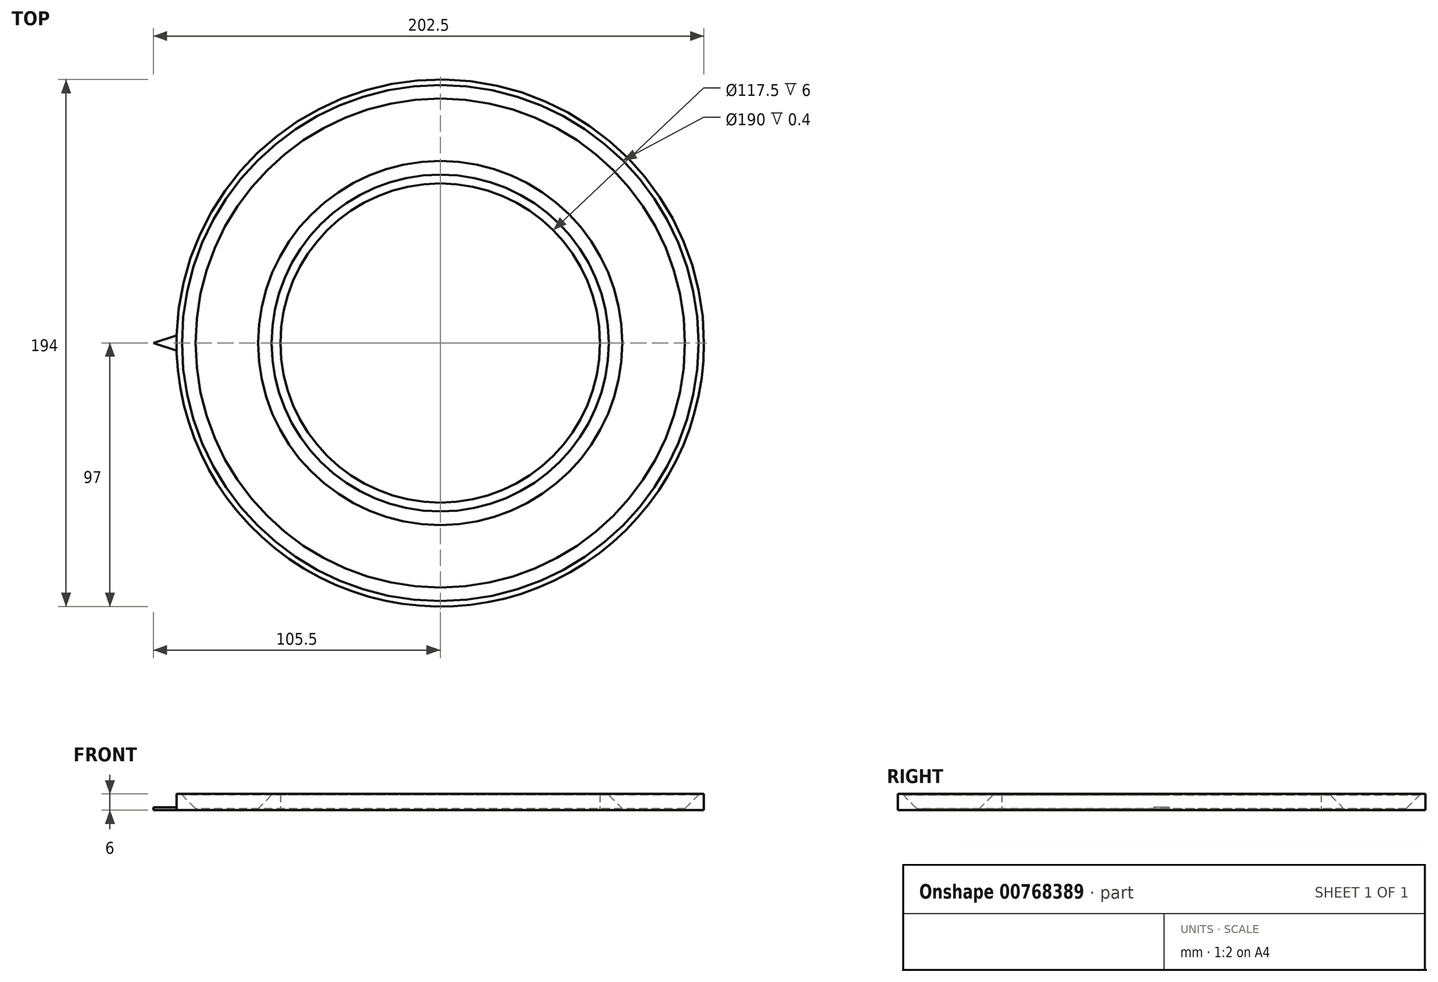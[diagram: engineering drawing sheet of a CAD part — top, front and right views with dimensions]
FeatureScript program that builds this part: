
annotation { "Feature Type Name" : "Feature", "Feature Type Description" : "" }
export const myFeature = defineFeature(function(context is Context, id is Id, definition is map)
    precondition{}
    {
        {
            var Q0;
            Q0=qCreatedBy(makeId("Top.planeOp"),FACE);
            var sketch = newSketch(context, id + "F0", { "sketchPlane" : qUnion([Q0])});
            skCircle(sketch, "E0", {"center": v(0, 0) * mm, "radius": 58.75 * mm});
            skCircle(sketch, "E1", {"center": v(0, 0) * mm, "radius": 62 * mm});
            skCircle(sketch, "E2", {"center": v(0, 0) * mm, "radius": 97 * mm});
            skCircle(sketch, "E3", {"center": v(0, 0) * mm, "radius": 95 * mm});
            skLineSegment(sketch, "E4", {"start": v(-97, 0) * mm, "end": v(-105.5, 0) * mm});
            skLineSegment(sketch, "E5", {"start": v(-105.5, 0) * mm, "end": v(-96.96, 2.84) * mm});
            skLineSegment(sketch, "E6", {"start": v(-105.5, 0) * mm, "end": v(-96.96, -2.84) * mm});
            skSolve(sketch);
        }
        {
            var Q0;
            Q0=makeQuery(id+"F0.imprint","IMPRINT",FACE,{"disambiguationData":[TD([[makeQuery(id+"F0.imprint","IMPRINT",EDGE,{"derivedFrom":sQuery(id+"F0.wireOp",EDGE,"E0")}),-1.0]])]});
            var Q1;
            Q1=makeQuery(id+"F0.imprint","IMPRINT",FACE,{"disambiguationData":[TD([[makeQuery(id+"F0.imprint","IMPRINT",EDGE,{"derivedFrom":sQuery(id+"F0.wireOp",EDGE,"E2")}),1.0]])]});
            var Q2;
            Q2=makeQuery(id+"F0.imprint","IMPRINT",FACE,{"disambiguationData":[TD([[makeQuery(id+"F0.imprint","IMPRINT",EDGE,{"derivedFrom":sQuery(id+"F0.wireOp",EDGE,"E1")}),-1.0]])]});
            extrude(context, id + "F1", {"entities" : qUnion([Q0, Q1, Q2]), "depth" : .6 * mm, "offsetDistance" : 25 * mm});
        }
        {
            var Q0;
            Q0=makeQuery(id+"F0.imprint","IMPRINT",FACE,{"disambiguationData":[TD([[makeQuery(id+"F0.imprint","IMPRINT",EDGE,{"derivedFrom":sQuery(id+"F0.wireOp",EDGE,"E2")}),1.0]])]});
            var Q1;
            Q1=makeQuery(id+"F0.imprint","IMPRINT",FACE,{"disambiguationData":[TD([[makeQuery(id+"F0.imprint","IMPRINT",EDGE,{"derivedFrom":sQuery(id+"F0.wireOp",EDGE,"E0")}),-1.0]])]});
            extrude(context, id + "F2", {"entities" : qUnion([Q0, Q1]), "operationType" : NewBodyOperationType.ADD, "depth" : 6 * mm, "offsetDistance" : 25 * mm});
        }
        {
            var Q0;
            {var subQ0=sQuery(id+"F0.wireOp",EDGE,"E4");Q0=makeQuery(id+"F0.imprint","IMPRINT",FACE,{"disambiguationData":[TD([[makeQuery(id+"F0.imprint","IMPRINT",EDGE,{"derivedFrom":subQ0}),-1.0]])]});}
            var Q1;
            {var subQ0=sQuery(id+"F0.wireOp",EDGE,"E4");Q1=makeQuery(id+"F0.imprint","IMPRINT",FACE,{"disambiguationData":[TD([[makeQuery(id+"F0.imprint","IMPRINT",EDGE,{"derivedFrom":subQ0}),1.0]])]});}
            extrude(context, id + "F3", {"entities" : qUnion([Q0, Q1]), "operationType" : NewBodyOperationType.ADD, "depth" : 1 * mm, "offsetDistance" : 25 * mm});
        }
        {
            var Q0;
            Q0=makeQuery(id+"F2.boolean.opBoolean","INTERSECT",EDGE,{"derivedFrom":[makeQuery(id+"F1.opExtrude","CAP_FACE",FACE,{"disambiguationData":[OSD([sQuery(id+"F0.wireOp",EDGE,"E0"),sQuery(id+"F0.wireOp",EDGE,"E2")])],"isStart":false}),makeQuery(id+"F2.opExtrude","SWEPT_FACE",FACE,{"disambiguationData":[OSD([sQuery(id+"F0.wireOp",EDGE,"E1")])]})]});
            var Q1;
            Q1=makeQuery(id+"F2.boolean.opBoolean","INTERSECT",EDGE,{"derivedFrom":[makeQuery(id+"F1.opExtrude","CAP_FACE",FACE,{"disambiguationData":[OSD([sQuery(id+"F0.wireOp",EDGE,"E0"),sQuery(id+"F0.wireOp",EDGE,"E2")])],"isStart":false}),makeQuery(id+"F2.opExtrude","SWEPT_FACE",FACE,{"disambiguationData":[OSD([sQuery(id+"F0.wireOp",EDGE,"E3")])]})]});
            chamfer(context, id + "F4", {"entities" : qUnion([Q0, Q1]), "width" : 5 * mm, "tangentPropagation" : true});
        }
    });
